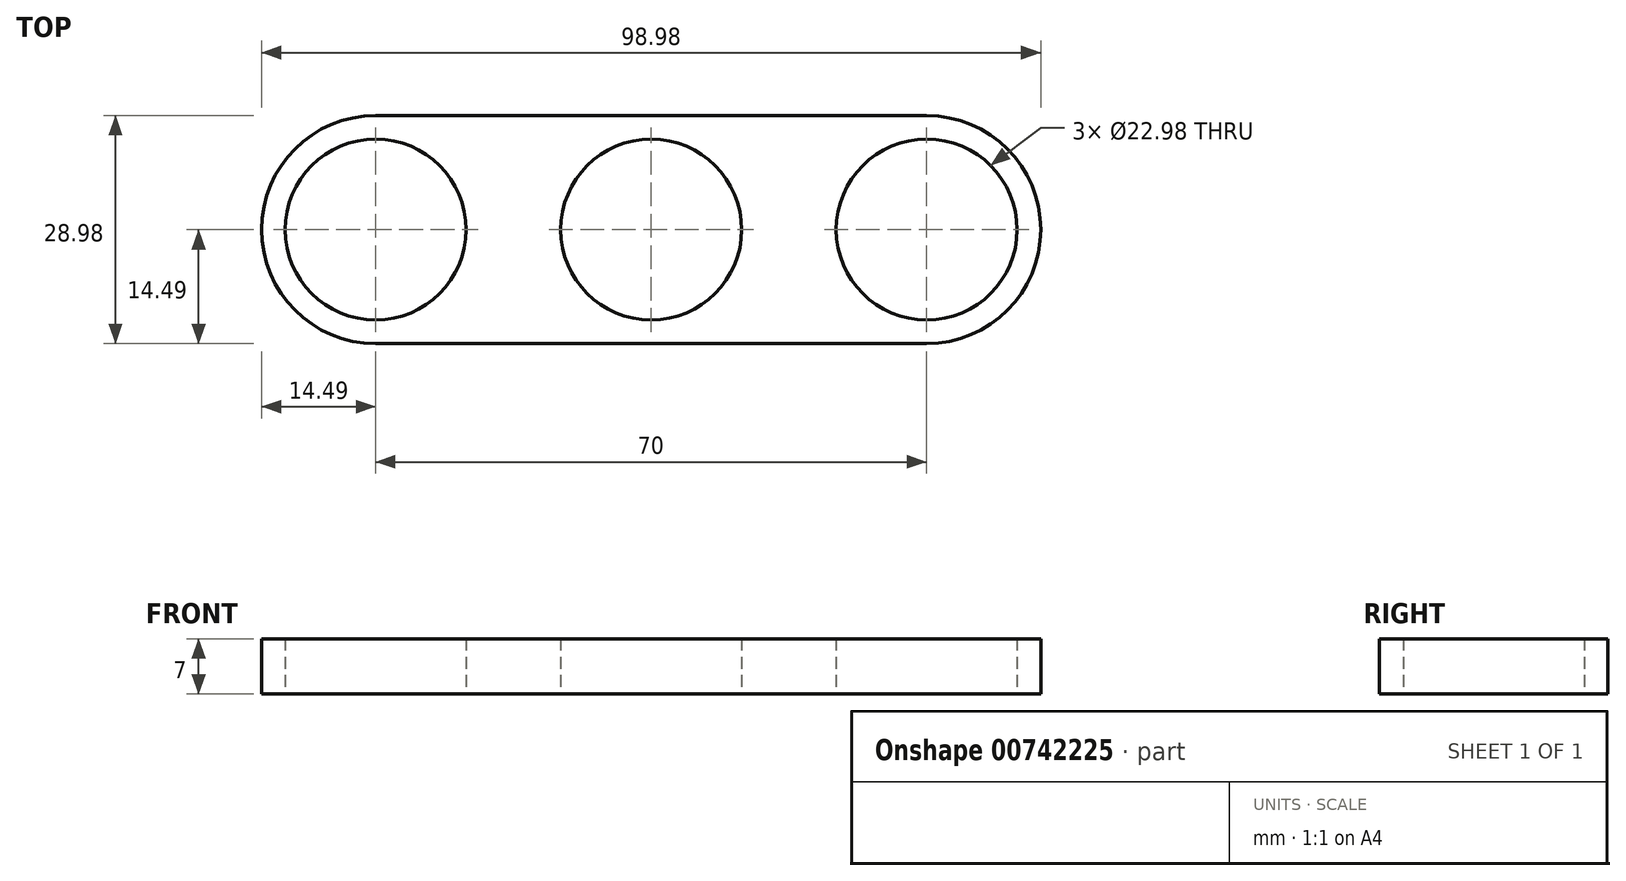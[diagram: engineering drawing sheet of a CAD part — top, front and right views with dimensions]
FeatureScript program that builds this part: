
annotation { "Feature Type Name" : "Feature", "Feature Type Description" : "" }
export const myFeature = defineFeature(function(context is Context, id is Id, definition is map)
    precondition{}
    {
        {
            var Q0;
            Q0=qCreatedBy(makeId("Top.planeOp"),FACE);
            var sketch = newSketch(context, id + "F0", { "sketchPlane" : qUnion([Q0])});
            skCircle(sketch, "E0", {"center": v(-35, 0) * mm, "radius": 11.5 * mm});
            skCircle(sketch, "E1", {"center": v(35, 0) * mm, "radius": 11.5 * mm});
            skCircle(sketch, "E2", {"center": v(0, 0) * mm, "radius": 11.5 * mm});
            skArc(sketch, "E3", {"start": v(-35, 14.5) * mm, "mid": v(-49.5, 0) * mm, "end": v(-35, -14.5) * mm});
            skArc(sketch, "E4", {"start": v(35, -14.5) * mm, "mid": v(49.5, 0) * mm, "end": v(35, 14.5) * mm});
            skLineSegment(sketch, "E5", {"start": v(-35, 14.49) * mm, "end": v(35, 14.5) * mm});
            skLineSegment(sketch, "E6", {"start": v(-35, -14.5) * mm, "end": v(35, -14.49) * mm});
            skSolve(sketch);
        }
        {
            var Q0;
            Q0=makeQuery(id+"F0.imprint","IMPRINT",FACE,{"disambiguationData":[TD([[makeQuery(id+"F0.imprint","IMPRINT",EDGE,{"derivedFrom":sQuery(id+"F0.wireOp",EDGE,"E0")}),-1.0]])]});
            extrude(context, id + "F1", {"entities" : qUnion([Q0]), "depth" : 7 * mm, "offsetDistance" : 25 * mm});
        }
    });
